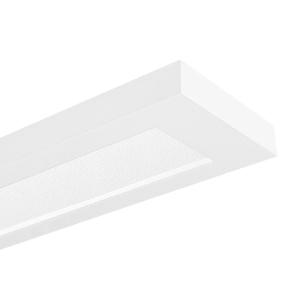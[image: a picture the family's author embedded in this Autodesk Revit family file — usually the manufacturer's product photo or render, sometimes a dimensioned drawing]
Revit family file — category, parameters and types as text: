
# Revit family: 3f_filippi_-_3f_travetta_di_lgs_3f_filippi_-_11633_-_3f_trav__led_di_2x30w-940_dali_lgs_l1590_dba5
name_source: partatom
category: Lighting Fixtures
units: mm (PartAtom-declared; Revit-internal decimal feet)

## family parameters
Cut with Voids When Loaded = No
Host = Face
Light Source = No
Part Type = Normal
Room Calculation Point = No
Round Connector Dimension = Use Diameter
Shared = No

## types (1)
- 3F Filippi - 3F Travetta DI LGS (1 x LED, 4963 lm, 66 W, 4000 K)
    Apparent Load = 66 VA
    Approval mark = ENEC
    CIE Flux Codes = 64 93 99 85 100
    Color Rendering = 90
    Color Temperature = 4000 K
    Control Gear = Electronic transformer
    Default Elevation = 1800 mm
    Description = ILLUMINOTECHNICAL
Luminous efficiency 100% (DLOR 85%, ULOR 15%).
Initial luminous flux of the luminaire 4963 lm.
Symmetric direct-indirect distribution.
Installation Interdistance Transv.D = 1.18 x hu - Long.D = 1.18 x hu.
Average luminance <3000 cd/m² for radial angles >65°.
Tabular UGR (CIE 117 - 4H-8H; S=0.25H; 70/50/20): RUG 17.2 - 17.7.
Beam angle: 89° - 91°.
Luminous efficacy 75 lm/W.
Lifetime (L93/B10): 30000 h. (tq+25°C)
Lifetime (L90/B10): 50000 h. (tq+25°C)
Lifetime (L85/B10): 80000 h. (tq+25°C)
Lifetime (L80/B10): 100000 h. (tq+25°C)
Sudden decreased luminous flux after 50000 hours: 0% (C0).
Photobiological safety in compliance with IEC/TR 62778: RG0 risk exempt, (IEC 62471).
In compliance with IEC/EN 62722-2-1 - IEC/EN 62717 standards.

SOURCE
2 linear LED modules 30W/940.
Energy efficiency class (UE 2019/2020 - UE 2019/2015): E.
CIE 13.3 Colour rendering index: CRI >90 (R9 >50%).
IES TM-30 Fidelity Index: Rf = 92 Rg = 101.
CCT nominal colour temperature 4000 K.
Colour initial tolerance (MacAdam): SDCM 2.

MECHANICAL
Housing with squared shape in white painted galvannealed steel, with nonreflecting surface.
Flow recuperator in semi-glossy aluminium.
LGS micro-prismatic flat diffuser in transparent methacrylate (PMMA), multi-lenticular exterior, anti-glare.
Anti-glare opal polycarbonate filter for brightness uniformity.
Upper holes closing film made of opal polycarbonate.
Luminaire with limited surface temperature. - D - (EN 60598-2-24)
Dimensions: 1590x190 mm, height 60 mm. Weight 5.6 kg.
IP20 protection degree.
Glow-wire test resistance 650°C.

ELECTRICAL
Halogen Free DALI-2 DATI (Parts 251, 252, 253), PUSH-DIM, electronic wiring 230V-50/60Hz, power factor 0.95 at full load, THD <25%, constant output current, SELV, class I, 1 driver, 1 DALI addresse.
Power of the luminaire 66 W.
CE - IEC 60598-1 - EN 60598-1.
SAFE FLICKER: PstLM=<1 and SVM=<0.4 (IEC TR 61547-1 and IEC TR 63158), to ensure a more comfortable and safe light.
Luminaire compliant with EN 60598-2-22 for power supply from a centralised emergency system CPSS (Central Power Supply System), not incorporated in the luminaire - high risk areas excluded. The default power and flux are 100% in AC and 15% in DC.
Ambient temperature from 0°C to +25°C.
Temperature class T6 max 85°C.
Relative humidity UR: <85%.

INSTALLATION
Suspended.
All accessories dedicated to this product are available on the Catalog and on our website www.3F-Filippi.com.

APPLICATIONS
In environments, even with reduced height, requiring a comfortable light.
In environments with VDTs, managerial offices and staterooms, public offices and schools.

LIGHT MANAGEMENT
Recommended minimum setting: 10%.
The luminaire, equipped with (DALI-2 DATI) driver, can be controlled manually with 3F Easy Dim technology or automatically/manually with wired or wireless DALI/D2D control systems.
The D2D driver guarantees interoperability with other devices with the same certification by making the following information available:
Device Data (Part 251), Energy Report (Part 252), Diagnosis & Maintenance (Part 253).
In electrical systems without a regulation system (manual or automatic) and DALI bus, a suitable jumper must be made on the DA-DA terminals of the appliance.

WARNING
Luminaire designed for disposal/recycling at end-of-life.
Replaceable (LED only) light source by a professional. Replaceable control gear by a professional.
    Height = 60 mm  [stored 0.19685 ft]
    Lamp = 1 x LED
    Lamp Light Flux = 4963 lm
    Lamp Power = 66 W
    Lamp count = 1
    Length = 1590 mm
    Lifetime = 50000 h
    Luminous efficacy = 75 lm/W
    Manufacturer = 3F Filippi
    ModVariant = No
    Model = 3F Filippi - 11633 - 3F Trav. LED DI 2x30W-940 DALI LGS L1590
    Mounting Place = Ceiling
    Mounting Type = Pendant
    Number of Poles = 1
    OnlyDefault = Yes
    Power Factor = 1
    Product Name = 3F Filippi - 3F Travetta DI LGS
    Product group = pendant luminaire
    ProductGroupID = 9
    Protection Class = Protection class I
    Protection Degree = IP 20
    RLX_Detail_Level = 1
    RLX_Emergency_Light_Flux = 0 lm
    RLX_Emergency_Type = 0
    RLX_Emergency_Type_DB = No
    RlxData = <blob elided: 52789 chars, md5=8f23fa0c>
    Socket = socket
    Standby Power = 0 W
    System Light Flux = 4963 lm
    System Power = 66 W
    Type Comments = Product without accessories
    Type Image = 3ffilippi_3f_travetta_led_lgs.jpg
    URL = http://relux.com
    VarID = ---
    Voltage = 0 V
    Weight = 0.00 kg
    Width = 190 mm  [stored 0.62336 ft]

note: [stored X ft] marks values corroborated as IEEE doubles in the binary element streams (Revit-internal decimal feet)

## geometry (parser evidence)
native form markers: Blend x4, Sweep x14
no freeform markers — native parametric forms only
